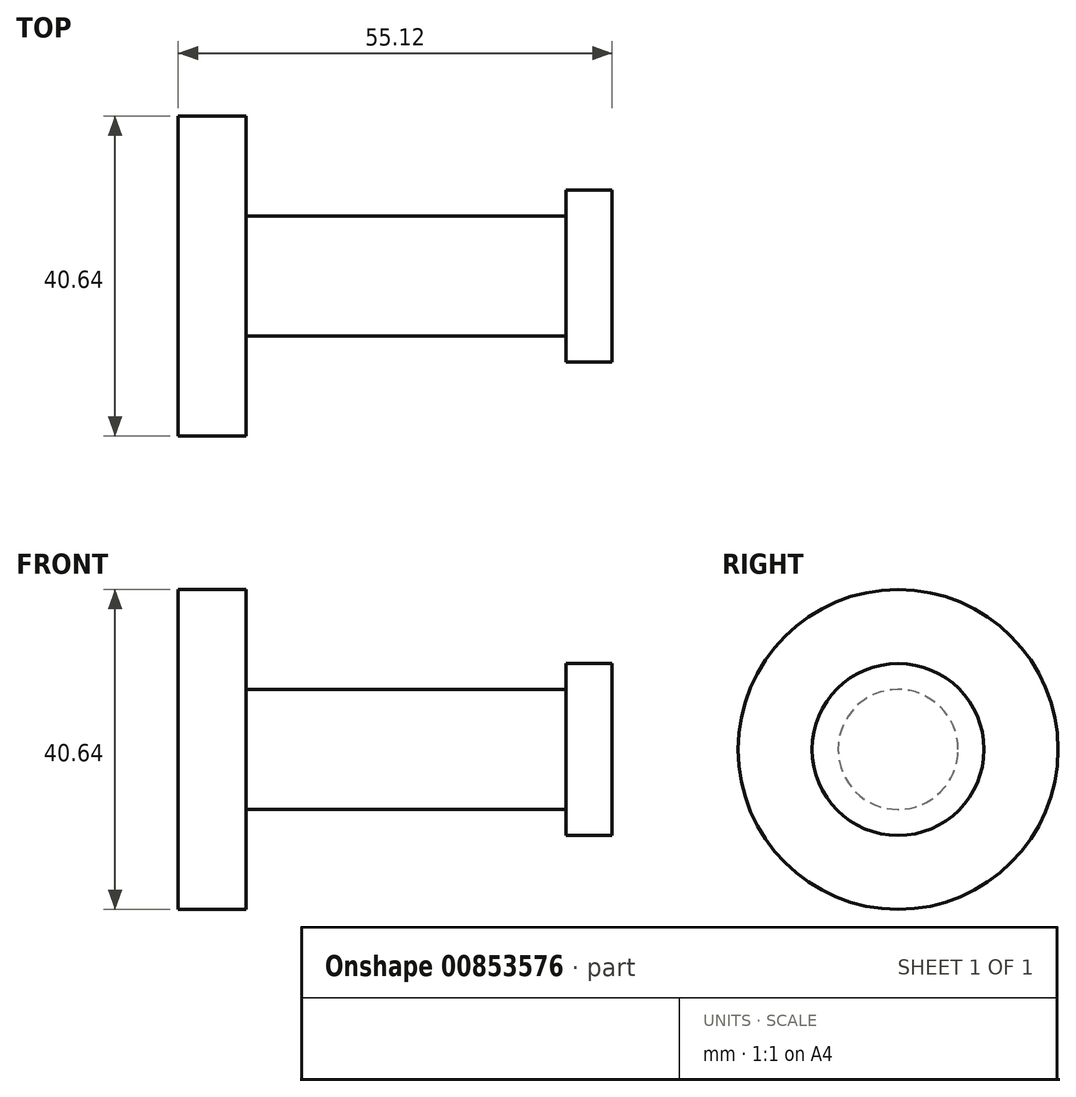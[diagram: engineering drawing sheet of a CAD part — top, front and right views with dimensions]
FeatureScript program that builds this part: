
annotation { "Feature Type Name" : "Feature", "Feature Type Description" : "" }
export const myFeature = defineFeature(function(context is Context, id is Id, definition is map)
    precondition{}
    {
        {
            var Q0;
            Q0=qCreatedBy(makeId("Front.planeOp"),FACE);
            var sketch = newSketch(context, id + "F0", { "sketchPlane" : qUnion([Q0])});
            skLineSegment(sketch, "E0", {"start": v(0, 0) * mm, "end": v(-134.9, 0) * mm, "construction": true});
            skLineSegment(sketch, "E1", {"start": v(0, 0) * mm, "end": v(0, 20.32) * mm});
            skLineSegment(sketch, "E2", {"start": v(0, 20.32) * mm, "end": v(8.64, 20.32) * mm});
            skLineSegment(sketch, "E3", {"start": v(8.64, 20.32) * mm, "end": v(8.64, 7.62) * mm});
            skLineSegment(sketch, "E4", {"start": v(8.64, 7.62) * mm, "end": v(49.28, 7.62) * mm});
            skLineSegment(sketch, "E5", {"start": v(49.28, 7.62) * mm, "end": v(49.28, 10.92) * mm});
            skLineSegment(sketch, "E6", {"start": v(49.28, 10.92) * mm, "end": v(55.12, 10.92) * mm});
            skLineSegment(sketch, "E7", {"start": v(55.12, 10.92) * mm, "end": v(55.12, 0) * mm});
            skLineSegment(sketch, "E8", {"start": v(55.12, 0) * mm, "end": v(0, 0) * mm});
            skSolve(sketch);
        }
        {
            var Q0;
            Q0 = qSketchRegion(id + "F0", true);
            var Q1;
            Q1=sQuery(id+"F0.wireOp",EDGE,"E0");
            revolve(context, id + "F1", {"surfaceOperationType" : NewSurfaceOperationType.NEW, "entities" : qUnion([Q0]), "axis" : qUnion([Q1]), "revolveType" : RevolveType.FULL});
        }
    });
